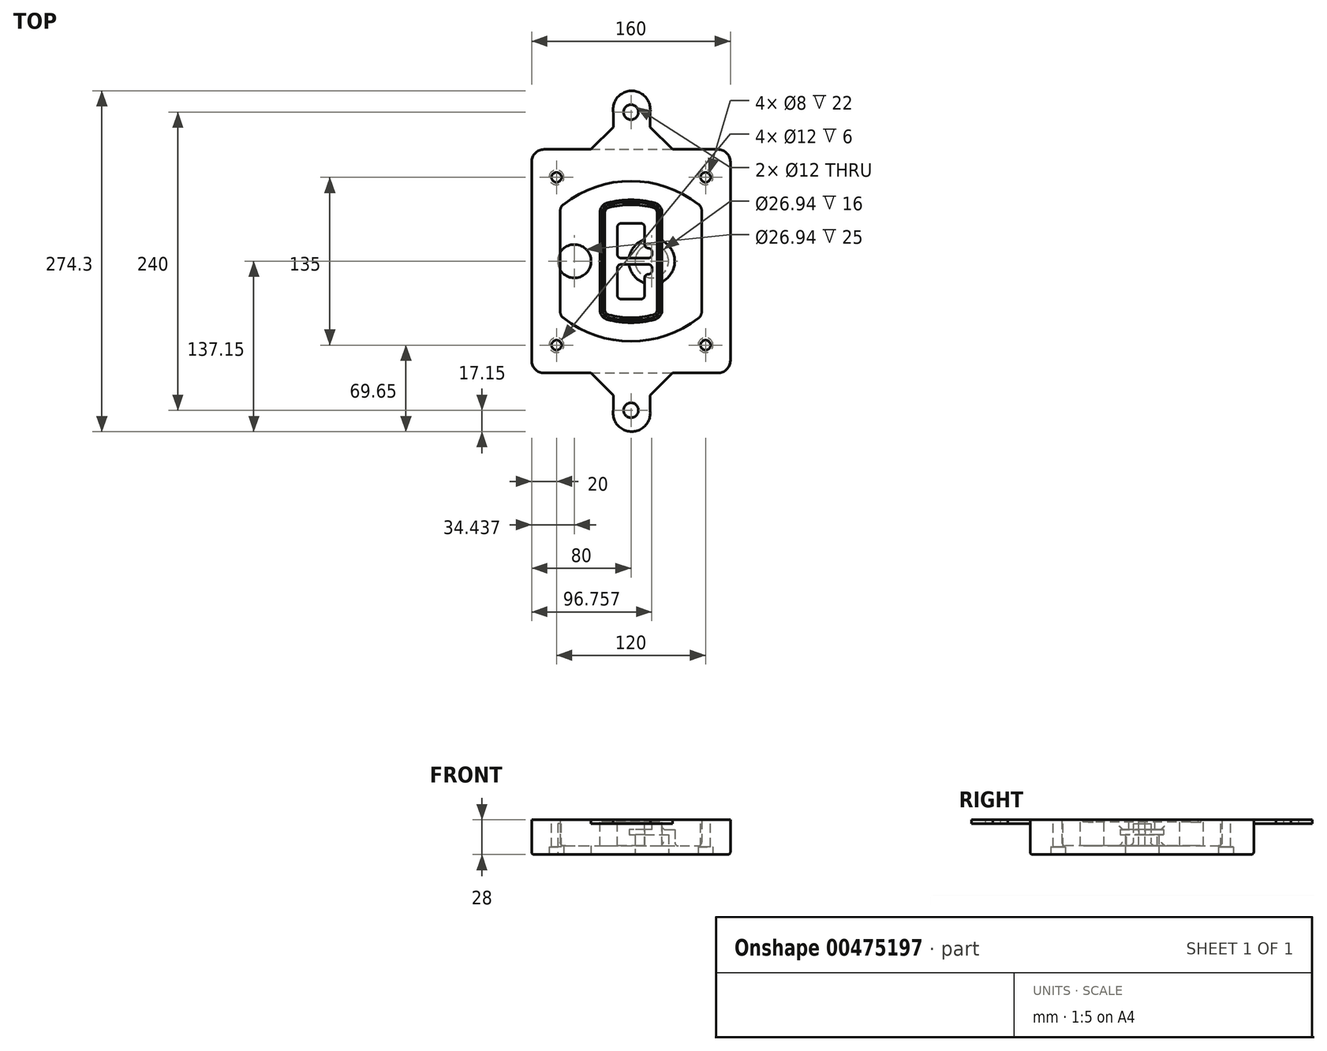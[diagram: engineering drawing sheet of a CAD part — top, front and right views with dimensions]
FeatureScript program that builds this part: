
annotation { "Feature Type Name" : "Feature", "Feature Type Description" : "" }
export const myFeature = defineFeature(function(context is Context, id is Id, definition is map)
    precondition{}
    {
        {
            var Q0;
            Q0=qCreatedBy(makeId("Top.planeOp"),FACE);
            var sketch = newSketch(context, id + "F0", { "sketchPlane" : qUnion([Q0])});
            skPoint(sketch, "E0.rect.middle", {"position": v(0, 0) * mm});
            skLineSegment(sketch, "E1.bottom", {"start": v(-70, -90) * mm, "end": v(70, -90) * mm});
            skLineSegment(sketch, "E1.top", {"start": v(-70, 90) * mm, "end": v(70, 90) * mm});
            skLineSegment(sketch, "E1.left", {"start": v(-80, -80) * mm, "end": v(-80, 80) * mm});
            skLineSegment(sketch, "E1.right", {"start": v(80, -80) * mm, "end": v(80, 80) * mm});
            skLineSegment(sketch, "E2", {"start": v(-80, 90) * mm, "end": v(80, -90) * mm, "construction": true});
            skLineSegment(sketch, "E3", {"start": v(80, 90) * mm, "end": v(-80, -90) * mm, "construction": true});
            skCircle(sketch, "E4", {"center": v(-60, 67.5) * mm, "radius": 4 * mm});
            skCircle(sketch, "E5", {"center": v(60, 67.5) * mm, "radius": 4 * mm});
            skCircle(sketch, "E6", {"center": v(60, -67.5) * mm, "radius": 4 * mm});
            skCircle(sketch, "E7", {"center": v(-60, -67.5) * mm, "radius": 4 * mm});
            skLineSegment(sketch, "E8", {"start": v(-60, 67.5) * mm, "end": v(60, 67.5) * mm, "construction": true});
            skLineSegment(sketch, "E9", {"start": v(60, 67.5) * mm, "end": v(60, -67.5) * mm, "construction": true});
            skLineSegment(sketch, "E10", {"start": v(60, -67.5) * mm, "end": v(-60, -67.5) * mm, "construction": true});
            skLineSegment(sketch, "E11", {"start": v(-60, -67.5) * mm, "end": v(-60, 67.5) * mm, "construction": true});
            skLineSegment(sketch, "E12", {"start": v(-60, 40.3) * mm, "end": v(-60, -40.3) * mm});
            skLineSegment(sketch, "E13", {"start": v(60, 40.3) * mm, "end": v(60, -40.3) * mm});
            skArc(sketch, "E14", {"start": v(56.15, 48.18) * mm, "mid": v(0, 67.5) * mm, "end": v(-56.15, 48.18) * mm});
            skArc(sketch, "E15", {"start": v(-56.15, -48.18) * mm, "mid": v(0, -67.5) * mm, "end": v(56.15, -48.18) * mm});
            skLineSegment(sketch, "E16", {"start": v(-60, 0) * mm, "end": v(60, 0) * mm, "construction": true});
            skPoint(sketch, "E17.visualSharp", {"position": v(-60, -45) * mm});
            skArc(sketch, "E17.filletArc", {"start": v(-60, -40.3) * mm, "mid": v(-58.99, -44.68) * mm, "end": v(-56.15, -48.18) * mm});
            skPoint(sketch, "E18.visualSharp", {"position": v(-60, 45) * mm});
            skArc(sketch, "E18.filletArc", {"start": v(-56.15, 48.18) * mm, "mid": v(-58.99, 44.68) * mm, "end": v(-60, 40.3) * mm});
            skPoint(sketch, "E19.visualSharp", {"position": v(60, 45) * mm});
            skArc(sketch, "E19.filletArc", {"start": v(60, 40.3) * mm, "mid": v(58.99, 44.68) * mm, "end": v(56.15, 48.18) * mm});
            skPoint(sketch, "E20.visualSharp", {"position": v(60, -45) * mm});
            skArc(sketch, "E20.filletArc", {"start": v(56.15, -48.18) * mm, "mid": v(58.99, -44.68) * mm, "end": v(60, -40.3) * mm});
            skPoint(sketch, "E21.visualSharp", {"position": v(-80, 90) * mm});
            skArc(sketch, "E21.filletArc", {"start": v(-70, 90) * mm, "mid": v(-77.07, 87.07) * mm, "end": v(-80, 80) * mm});
            skPoint(sketch, "E22.visualSharp", {"position": v(80, 90) * mm});
            skArc(sketch, "E22.filletArc", {"start": v(80, 80) * mm, "mid": v(77.07, 87.07) * mm, "end": v(70, 90) * mm});
            skPoint(sketch, "E23.visualSharp", {"position": v(80, -90) * mm});
            skArc(sketch, "E23.filletArc", {"start": v(70, -90) * mm, "mid": v(77.07, -87.07) * mm, "end": v(80, -80) * mm});
            skPoint(sketch, "E24.visualSharp", {"position": v(-80, -90) * mm});
            skArc(sketch, "E24.filletArc", {"start": v(-80, -80) * mm, "mid": v(-77.07, -87.07) * mm, "end": v(-70, -90) * mm});
            skArc(sketch, "E25.0", {"start": v(57, 40.3) * mm, "mid": v(56.3, 43.36) * mm, "end": v(54.3, 45.81) * mm});
            skLineSegment(sketch, "E25.1", {"start": v(57, 40.3) * mm, "end": v(57, -40.3) * mm});
            skArc(sketch, "E25.2", {"start": v(54.3, -45.81) * mm, "mid": v(56.3, -43.36) * mm, "end": v(57, -40.3) * mm});
            skArc(sketch, "E25.3", {"start": v(-54.3, -45.81) * mm, "mid": v(0, -64.5) * mm, "end": v(54.3, -45.81) * mm});
            skArc(sketch, "E25.4", {"start": v(-57, -40.3) * mm, "mid": v(-56.3, -43.36) * mm, "end": v(-54.3, -45.81) * mm});
            skArc(sketch, "E25.5", {"start": v(54.3, 45.81) * mm, "mid": v(0, 64.5) * mm, "end": v(-54.3, 45.81) * mm});
            skLineSegment(sketch, "E25.6", {"start": v(-57, 40.3) * mm, "end": v(-57, -40.3) * mm});
            skArc(sketch, "E25.7", {"start": v(-54.3, 45.81) * mm, "mid": v(-56.3, 43.36) * mm, "end": v(-57, 40.3) * mm});
            skArc(sketch, "E26.0", {"start": v(-58.62, 51.33) * mm, "mid": v(-62.58, 46.43) * mm, "end": v(-64, 40.3) * mm});
            skArc(sketch, "E26.1", {"start": v(58.62, 51.33) * mm, "mid": v(0, 71.5) * mm, "end": v(-58.62, 51.33) * mm});
            skArc(sketch, "E26.2", {"start": v(64, 40.3) * mm, "mid": v(62.58, 46.43) * mm, "end": v(58.62, 51.33) * mm});
            skLineSegment(sketch, "E26.3", {"start": v(64, 40.3) * mm, "end": v(64, -40.3) * mm});
            skArc(sketch, "E26.4", {"start": v(58.62, -51.33) * mm, "mid": v(62.58, -46.43) * mm, "end": v(64, -40.3) * mm});
            skLineSegment(sketch, "E26.5", {"start": v(-64, 40.3) * mm, "end": v(-64, -40.3) * mm});
            skArc(sketch, "E26.6", {"start": v(-58.62, -51.33) * mm, "mid": v(0, -71.5) * mm, "end": v(58.62, -51.33) * mm});
            skArc(sketch, "E26.7", {"start": v(-64, -40.3) * mm, "mid": v(-62.58, -46.43) * mm, "end": v(-58.62, -51.33) * mm});
            skSolve(sketch);
        }
        {
            var Q0;
            Q0=makeQuery(id+"F0.imprint","IMPRINT",FACE,{"disambiguationData":[TD([[makeQuery(id+"F0.imprint","IMPRINT",EDGE,{"derivedFrom":sQuery(id+"F0.wireOp",EDGE,"E1.bottom")}),1.0]])]});
            var Q1;
            Q1=makeQuery(id+"F0.imprint","IMPRINT",FACE,{"disambiguationData":[TD([[makeQuery(id+"F0.imprint","IMPRINT",EDGE,{"derivedFrom":sQuery(id+"F0.wireOp",EDGE,"E12")}),1.0]])]});
            var Q2;
            Q2=makeQuery(id+"F0.imprint","IMPRINT",FACE,{"disambiguationData":[TD([[makeQuery(id+"F0.imprint","IMPRINT",EDGE,{"derivedFrom":sQuery(id+"F0.wireOp",EDGE,"E25.0")}),1.0]])]});
            var Q3;
            Q3=makeQuery(id+"F0.imprint","IMPRINT",FACE,{"disambiguationData":[TD([[makeQuery(id+"F0.imprint","IMPRINT",EDGE,{"derivedFrom":sQuery(id+"F0.wireOp",EDGE,"E12")}),-1.0]])]});
            extrude(context, id + "F1", {"entities" : qUnion([Q0, Q1, Q2, Q3]), "oppositeDirection" : true, "depth" : 25 * mm});
        }
        {
            var Q0;
            Q0=makeQuery(id+"F0.imprint","IMPRINT",FACE,{"disambiguationData":[TD([[makeQuery(id+"F0.imprint","IMPRINT",EDGE,{"derivedFrom":sQuery(id+"F0.wireOp",EDGE,"E12")}),1.0]])]});
            extrude(context, id + "F2", {"entities" : qUnion([Q0]), "operationType" : NewBodyOperationType.ADD, "depth" : 3 * mm});
        }
        {
            var Q0;
            Q0=makeQuery(id+"F0.imprint","IMPRINT",FACE,{"disambiguationData":[TD([[makeQuery(id+"F0.imprint","IMPRINT",EDGE,{"derivedFrom":sQuery(id+"F0.wireOp",EDGE,"E25.0")}),1.0]])]});
            extrude(context, id + "F3", {"entities" : qUnion([Q0]), "operationType" : NewBodyOperationType.REMOVE, "oppositeDirection" : true, "depth" : 18 * mm});
        }
        {
            var Q0;
            Q0=makeQuery(id+"F2.opExtrude","CAP_FACE",FACE,{"disambiguationData":[OSD([sQuery(id+"F0.wireOp",EDGE,"E12"),sQuery(id+"F0.wireOp",EDGE,"E13"),sQuery(id+"F0.wireOp",EDGE,"E14"),sQuery(id+"F0.wireOp",EDGE,"E15"),sQuery(id+"F0.wireOp",EDGE,"E17.filletArc"),sQuery(id+"F0.wireOp",EDGE,"E18.filletArc"),sQuery(id+"F0.wireOp",EDGE,"E19.filletArc"),sQuery(id+"F0.wireOp",EDGE,"E20.filletArc"),sQuery(id+"F0.wireOp",EDGE,"E25.0"),sQuery(id+"F0.wireOp",EDGE,"E25.1"),sQuery(id+"F0.wireOp",EDGE,"E25.2"),sQuery(id+"F0.wireOp",EDGE,"E25.3"),sQuery(id+"F0.wireOp",EDGE,"E25.4"),sQuery(id+"F0.wireOp",EDGE,"E25.5"),sQuery(id+"F0.wireOp",EDGE,"E25.6"),sQuery(id+"F0.wireOp",EDGE,"E25.7")])],"isStart":false});
            var sketch = newSketch(context, id + "F4", { "sketchPlane" : qUnion([Q0])});
            skArc(sketch, "E27.0", {"start": v(-19.08, -46.97) * mm, "mid": v(0, -49.5) * mm, "end": v(19.08, -46.97) * mm});
            skArc(sketch, "E28.0", {"start": v(19.08, 46.97) * mm, "mid": v(0, 49.5) * mm, "end": v(-19.08, 46.97) * mm});
            skLineSegment(sketch, "E29", {"start": v(-25, 39.25) * mm, "end": v(-25, -39.25) * mm});
            skLineSegment(sketch, "E30", {"start": v(25, 39.25) * mm, "end": v(25, -39.25) * mm});
            skLineSegment(sketch, "E31", {"start": v(-25, 45.1) * mm, "end": v(25, 45.1) * mm, "construction": true});
            skLineSegment(sketch, "E32", {"start": v(-25, -45.1) * mm, "end": v(25, -45.1) * mm, "construction": true});
            skPoint(sketch, "E33.visualSharp", {"position": v(-25, 45.1) * mm});
            skArc(sketch, "E33.filletArc", {"start": v(-19.08, 46.97) * mm, "mid": v(-23.35, 44.11) * mm, "end": v(-25, 39.25) * mm});
            skPoint(sketch, "E34.visualSharp", {"position": v(25, 45.1) * mm});
            skArc(sketch, "E34.filletArc", {"start": v(25, 39.25) * mm, "mid": v(23.35, 44.11) * mm, "end": v(19.08, 46.97) * mm});
            skPoint(sketch, "E35.visualSharp", {"position": v(25, -45.1) * mm});
            skArc(sketch, "E35.filletArc", {"start": v(19.08, -46.97) * mm, "mid": v(23.35, -44.11) * mm, "end": v(25, -39.25) * mm});
            skPoint(sketch, "E36.visualSharp", {"position": v(-25, -45.1) * mm});
            skArc(sketch, "E36.filletArc", {"start": v(-25, -39.25) * mm, "mid": v(-23.35, -44.11) * mm, "end": v(-19.08, -46.97) * mm});
            skArc(sketch, "E37.0", {"start": v(54.3, 45.81) * mm, "mid": v(0, 64.5) * mm, "end": v(-54.3, 45.81) * mm});
            skArc(sketch, "E37.1", {"start": v(-54.3, 45.81) * mm, "mid": v(-56.3, 43.36) * mm, "end": v(-57, 40.3) * mm});
            skLineSegment(sketch, "E37.2", {"start": v(-57, 40.3) * mm, "end": v(-57, -40.3) * mm});
            skArc(sketch, "E37.3", {"start": v(-57, -40.3) * mm, "mid": v(-56.3, -43.36) * mm, "end": v(-54.3, -45.81) * mm});
            skArc(sketch, "E37.4", {"start": v(-54.3, -45.81) * mm, "mid": v(0, -64.5) * mm, "end": v(54.3, -45.81) * mm});
            skArc(sketch, "E37.5", {"start": v(54.3, -45.81) * mm, "mid": v(56.3, -43.36) * mm, "end": v(57, -40.3) * mm});
            skLineSegment(sketch, "E37.6", {"start": v(57, 40.3) * mm, "end": v(57, -40.3) * mm});
            skArc(sketch, "E37.7", {"start": v(57, 40.3) * mm, "mid": v(56.3, 43.36) * mm, "end": v(54.3, 45.81) * mm});
            skLineSegment(sketch, "E38.0", {"start": v(23, 39.25) * mm, "end": v(23, -39.25) * mm});
            skArc(sketch, "E38.1", {"start": v(18.56, -45.04) * mm, "mid": v(21.76, -42.9) * mm, "end": v(23, -39.25) * mm});
            skArc(sketch, "E38.2", {"start": v(-18.56, -45.04) * mm, "mid": v(0, -47.5) * mm, "end": v(18.56, -45.04) * mm});
            skArc(sketch, "E38.3", {"start": v(-23, -39.25) * mm, "mid": v(-21.76, -42.9) * mm, "end": v(-18.56, -45.04) * mm});
            skLineSegment(sketch, "E38.4", {"start": v(-23, 39.25) * mm, "end": v(-23, -39.25) * mm});
            skArc(sketch, "E38.5", {"start": v(23, 39.25) * mm, "mid": v(21.76, 42.9) * mm, "end": v(18.56, 45.04) * mm});
            skArc(sketch, "E38.6", {"start": v(-18.56, 45.04) * mm, "mid": v(-21.76, 42.9) * mm, "end": v(-23, 39.25) * mm});
            skArc(sketch, "E38.7", {"start": v(18.56, 45.04) * mm, "mid": v(0, 47.5) * mm, "end": v(-18.56, 45.04) * mm});
            skArc(sketch, "E39.0", {"start": v(21, 39.25) * mm, "mid": v(20.18, 41.68) * mm, "end": v(18.04, 43.1) * mm});
            skLineSegment(sketch, "E39.1", {"start": v(21, 39.25) * mm, "end": v(21, -39.25) * mm});
            skArc(sketch, "E39.2", {"start": v(18.04, -43.1) * mm, "mid": v(20.18, -41.68) * mm, "end": v(21, -39.25) * mm});
            skArc(sketch, "E39.3", {"start": v(-18.04, -43.1) * mm, "mid": v(0, -45.5) * mm, "end": v(18.04, -43.1) * mm});
            skArc(sketch, "E39.4", {"start": v(-21, -39.25) * mm, "mid": v(-20.18, -41.68) * mm, "end": v(-18.04, -43.1) * mm});
            skArc(sketch, "E39.5", {"start": v(18.04, 43.1) * mm, "mid": v(0, 45.5) * mm, "end": v(-18.04, 43.1) * mm});
            skLineSegment(sketch, "E39.6", {"start": v(-21, 39.25) * mm, "end": v(-21, -39.25) * mm});
            skArc(sketch, "E39.7", {"start": v(-18.04, 43.1) * mm, "mid": v(-20.18, 41.68) * mm, "end": v(-21, 39.25) * mm});
            skLineSegment(sketch, "E40", {"start": v(-25, 0) * mm, "end": v(25, 0) * mm, "construction": true});
            skLineSegment(sketch, "E41", {"start": v(-11, 5.5) * mm, "end": v(-11, 27.5) * mm});
            skLineSegment(sketch, "E42", {"start": v(-8, 30.5) * mm, "end": v(8, 30.5) * mm});
            skLineSegment(sketch, "E43", {"start": v(11, 27.5) * mm, "end": v(11, 13.5) * mm});
            skLineSegment(sketch, "E44", {"start": v(14, 10.5) * mm, "end": v(14, 10.5) * mm});
            skLineSegment(sketch, "E45", {"start": v(17, 7.5) * mm, "end": v(17, 5.5) * mm});
            skLineSegment(sketch, "E46", {"start": v(14, 2.5) * mm, "end": v(-8, 2.5) * mm});
            skPoint(sketch, "E47.visualSharp", {"position": v(-11, 30.5) * mm});
            skArc(sketch, "E47.filletArc", {"start": v(-8, 30.5) * mm, "mid": v(-10.12, 29.62) * mm, "end": v(-11, 27.5) * mm});
            skPoint(sketch, "E48.visualSharp", {"position": v(11, 30.5) * mm});
            skArc(sketch, "E48.filletArc", {"start": v(11, 27.5) * mm, "mid": v(10.12, 29.62) * mm, "end": v(8, 30.5) * mm});
            skPoint(sketch, "E49.visualSharp", {"position": v(11, 10.5) * mm});
            skArc(sketch, "E49.filletArc", {"start": v(11, 13.5) * mm, "mid": v(11.88, 11.38) * mm, "end": v(14, 10.5) * mm});
            skPoint(sketch, "E50.visualSharp", {"position": v(17, 10.5) * mm});
            skArc(sketch, "E50.filletArc", {"start": v(17, 7.5) * mm, "mid": v(16.12, 9.62) * mm, "end": v(14, 10.5) * mm});
            skPoint(sketch, "E51.visualSharp", {"position": v(17, 2.5) * mm});
            skArc(sketch, "E51.filletArc", {"start": v(14, 2.5) * mm, "mid": v(16.12, 3.38) * mm, "end": v(17, 5.5) * mm});
            skPoint(sketch, "E52.visualSharp", {"position": v(-11, 2.5) * mm});
            skArc(sketch, "E52.filletArc", {"start": v(-11, 5.5) * mm, "mid": v(-10.12, 3.38) * mm, "end": v(-8, 2.5) * mm});
            skLineSegment(sketch, "E53.0.MirrorCS", {"start": v(14, -2.5) * mm, "end": v(-8, -2.5) * mm});
            skArc(sketch, "E54.0.MirrorCS", {"start": v(-11, -5.5) * mm, "mid": v(-10.12, -3.38) * mm, "end": v(-8, -2.5) * mm});
            skLineSegment(sketch, "E55.0.MirrorCS", {"start": v(-11, -5.5) * mm, "end": v(-11, -27.5) * mm});
            skArc(sketch, "E56.0.MirrorCS", {"start": v(-8, -30.5) * mm, "mid": v(-10.12, -29.62) * mm, "end": v(-11, -27.5) * mm});
            skLineSegment(sketch, "E57.0.MirrorCS", {"start": v(-8, -30.5) * mm, "end": v(8, -30.5) * mm});
            skArc(sketch, "E58.0.MirrorCS", {"start": v(11, -27.5) * mm, "mid": v(10.12, -29.62) * mm, "end": v(8, -30.5) * mm});
            skLineSegment(sketch, "E59.0.MirrorCS", {"start": v(11, -27.5) * mm, "end": v(11, -13.5) * mm});
            skArc(sketch, "E60.0.MirrorCS", {"start": v(11, -13.5) * mm, "mid": v(11.88, -11.38) * mm, "end": v(14, -10.5) * mm});
            skArc(sketch, "E61.0.MirrorCS", {"start": v(17, -7.5) * mm, "mid": v(16.12, -9.62) * mm, "end": v(14, -10.5) * mm});
            skLineSegment(sketch, "E62.0.MirrorCS", {"start": v(17, -7.5) * mm, "end": v(17, -5.5) * mm});
            skArc(sketch, "E63.0.MirrorCS", {"start": v(14, -2.5) * mm, "mid": v(16.12, -3.38) * mm, "end": v(17, -5.5) * mm});
            skSolve(sketch);
        }
        {
            var Q0;
            Q0=makeQuery(id+"F4.imprint","IMPRINT",FACE,{"disambiguationData":[TD([[makeQuery(id+"F4.imprint","IMPRINT",EDGE,{"derivedFrom":sQuery(id+"F4.wireOp",EDGE,"E27.0")}),1.0]])]});
            var Q1;
            Q1=makeQuery(id+"F4.imprint","IMPRINT",FACE,{"disambiguationData":[TD([[makeQuery(id+"F4.imprint","IMPRINT",EDGE,{"derivedFrom":sQuery(id+"F4.wireOp",EDGE,"E38.0")}),-1.0]])]});
            var Q2;
            Q2=makeQuery(id+"F4.imprint","IMPRINT",FACE,{"disambiguationData":[TD([[makeQuery(id+"F4.imprint","IMPRINT",EDGE,{"derivedFrom":sQuery(id+"F4.wireOp",EDGE,"E39.0")}),1.0]])]});
            extrude(context, id + "F5", {"entities" : qUnion([Q0, Q1, Q2]), "operationType" : NewBodyOperationType.ADD, "endBound" : BoundingType.UP_TO_NEXT, "oppositeDirection" : true, "depth" : 25 * mm});
        }
        {
            var Q0;
            Q0=makeQuery(id+"F4.imprint","IMPRINT",FACE,{"disambiguationData":[TD([[makeQuery(id+"F4.imprint","IMPRINT",EDGE,{"derivedFrom":sQuery(id+"F4.wireOp",EDGE,"E38.0")}),-1.0]])]});
            extrude(context, id + "F6", {"entities" : qUnion([Q0]), "operationType" : NewBodyOperationType.REMOVE, "oppositeDirection" : true, "depth" : 2 * mm});
        }
        {
            var Q0;
            Q0=makeQuery(id+"F1.opExtrude","CAP_FACE",FACE,{"disambiguationData":[OSD([sQuery(id+"F0.wireOp",EDGE,"E1.bottom"),sQuery(id+"F0.wireOp",EDGE,"E1.top"),sQuery(id+"F0.wireOp",EDGE,"E1.left"),sQuery(id+"F0.wireOp",EDGE,"E1.right"),sQuery(id+"F0.wireOp",EDGE,"E4"),sQuery(id+"F0.wireOp",EDGE,"E5"),sQuery(id+"F0.wireOp",EDGE,"E6"),sQuery(id+"F0.wireOp",EDGE,"E7"),sQuery(id+"F0.wireOp",EDGE,"E21.filletArc"),sQuery(id+"F0.wireOp",EDGE,"E22.filletArc"),sQuery(id+"F0.wireOp",EDGE,"E23.filletArc"),sQuery(id+"F0.wireOp",EDGE,"E24.filletArc")])],"isStart":false});
            var sketch = newSketch(context, id + "F7", { "sketchPlane" : qUnion([Q0])});
            skCircle(sketch, "E64", {"center": v(16.76, 0) * mm, "radius": 13.47 * mm});
            skCircle(sketch, "E65", {"center": v(-45.56, 0) * mm, "radius": 13.47 * mm});
            skLineSegment(sketch, "E66", {"start": v(80, 0) * mm, "end": v(-80, 0) * mm});
            skCircle(sketch, "E67", {"center": v(16.76, 0) * mm, "radius": 18.47 * mm});
            skCircle(sketch, "E68", {"center": v(60, -67.5) * mm, "radius": 6 * mm});
            skCircle(sketch, "E69", {"center": v(-60, -67.5) * mm, "radius": 6 * mm});
            skCircle(sketch, "E70", {"center": v(-60, 67.5) * mm, "radius": 6 * mm});
            skCircle(sketch, "E71", {"center": v(60, 67.5) * mm, "radius": 6 * mm});
            skSolve(sketch);
        }
        {
            var Q0;
            {var subQ1=sQuery(id+"F7.wireOp",EDGE,"E66");var subQ4=sQuery(id+"F7.wireOp",EDGE,"E64");var subQ6=makeQuery(id+"F7.imprint","INTERSECT",VERTEX,{"disambiguationData":[OD(0.0)],"derivedFrom":[subQ4,subQ1]});Q0=makeQuery(id+"F7.imprint","IMPRINT",FACE,{"disambiguationData":[TD([[makeQuery(id+"F7.imprint","IMPRINT",EDGE,{"disambiguationData":[TD([[subQ6,-1.0]])],"derivedFrom":subQ4}),-1.0]])]});}
            var Q1;
            {var subQ0=sQuery(id+"F7.wireOp",EDGE,"E66");var subQ1=sQuery(id+"F7.wireOp",EDGE,"E64");var subQ3=makeQuery(id+"F7.imprint","INTERSECT",VERTEX,{"disambiguationData":[OD(0.0)],"derivedFrom":[subQ1,subQ0]});Q1=makeQuery(id+"F7.imprint","IMPRINT",FACE,{"disambiguationData":[TD([[makeQuery(id+"F7.imprint","IMPRINT",EDGE,{"disambiguationData":[TD([[subQ3,-1.0]])],"derivedFrom":subQ1}),1.0]])]});}
            var Q2;
            {var subQ0=sQuery(id+"F7.wireOp",EDGE,"E66");var subQ1=sQuery(id+"F7.wireOp",EDGE,"E64");var subQ3=makeQuery(id+"F7.imprint","INTERSECT",VERTEX,{"disambiguationData":[OD(0.0)],"derivedFrom":[subQ1,subQ0]});Q2=makeQuery(id+"F7.imprint","IMPRINT",FACE,{"disambiguationData":[TD([[makeQuery(id+"F7.imprint","IMPRINT",EDGE,{"disambiguationData":[TD([[subQ3,1.0]])],"derivedFrom":subQ1}),1.0]])]});}
            var Q3;
            {var subQ1=sQuery(id+"F7.wireOp",EDGE,"E66");var subQ4=sQuery(id+"F7.wireOp",EDGE,"E64");var subQ6=makeQuery(id+"F7.imprint","INTERSECT",VERTEX,{"disambiguationData":[OD(0.0)],"derivedFrom":[subQ4,subQ1]});Q3=makeQuery(id+"F7.imprint","IMPRINT",FACE,{"disambiguationData":[TD([[makeQuery(id+"F7.imprint","IMPRINT",EDGE,{"disambiguationData":[TD([[subQ6,1.0]])],"derivedFrom":subQ4}),-1.0]])]});}
            extrude(context, id + "F8", {"entities" : qUnion([Q0, Q1, Q2, Q3]), "operationType" : NewBodyOperationType.ADD, "oppositeDirection" : true, "depth" : 20 * mm});
        }
        {
            var Q0;
            {var subQ0=sQuery(id+"F7.wireOp",EDGE,"E66");var subQ1=sQuery(id+"F7.wireOp",EDGE,"E64");var subQ3=makeQuery(id+"F7.imprint","INTERSECT",VERTEX,{"disambiguationData":[OD(0.0)],"derivedFrom":[subQ1,subQ0]});Q0=makeQuery(id+"F7.imprint","IMPRINT",FACE,{"disambiguationData":[TD([[makeQuery(id+"F7.imprint","IMPRINT",EDGE,{"disambiguationData":[TD([[subQ3,-1.0]])],"derivedFrom":subQ1}),1.0]])]});}
            var Q1;
            {var subQ0=sQuery(id+"F7.wireOp",EDGE,"E66");var subQ1=sQuery(id+"F7.wireOp",EDGE,"E64");var subQ3=makeQuery(id+"F7.imprint","INTERSECT",VERTEX,{"disambiguationData":[OD(0.0)],"derivedFrom":[subQ1,subQ0]});Q1=makeQuery(id+"F7.imprint","IMPRINT",FACE,{"disambiguationData":[TD([[makeQuery(id+"F7.imprint","IMPRINT",EDGE,{"disambiguationData":[TD([[subQ3,1.0]])],"derivedFrom":subQ1}),1.0]])]});}
            extrude(context, id + "F9", {"entities" : qUnion([Q0, Q1]), "operationType" : NewBodyOperationType.REMOVE, "oppositeDirection" : true, "depth" : 16 * mm});
        }
        {
            var Q0;
            {var subQ0=sQuery(id+"F7.wireOp",EDGE,"E66");var subQ1=sQuery(id+"F7.wireOp",EDGE,"E65");var subQ3=makeQuery(id+"F7.imprint","INTERSECT",VERTEX,{"disambiguationData":[OD(0.0)],"derivedFrom":[subQ1,subQ0]});Q0=makeQuery(id+"F7.imprint","IMPRINT",FACE,{"disambiguationData":[TD([[makeQuery(id+"F7.imprint","IMPRINT",EDGE,{"disambiguationData":[TD([[subQ3,-1.0]])],"derivedFrom":subQ1}),1.0]])]});}
            var Q1;
            {var subQ0=sQuery(id+"F7.wireOp",EDGE,"E66");var subQ1=sQuery(id+"F7.wireOp",EDGE,"E65");var subQ3=makeQuery(id+"F7.imprint","INTERSECT",VERTEX,{"disambiguationData":[OD(0.0)],"derivedFrom":[subQ1,subQ0]});Q1=makeQuery(id+"F7.imprint","IMPRINT",FACE,{"disambiguationData":[TD([[makeQuery(id+"F7.imprint","IMPRINT",EDGE,{"disambiguationData":[TD([[subQ3,1.0]])],"derivedFrom":subQ1}),1.0]])]});}
            extrude(context, id + "F10", {"entities" : qUnion([Q0, Q1]), "operationType" : NewBodyOperationType.REMOVE, "oppositeDirection" : true, "depth" : 25 * mm});
        }
        {
            var Q0;
            Q0=makeQuery(id+"F7.imprint","IMPRINT",FACE,{"disambiguationData":[TD([[makeQuery(id+"F7.imprint","IMPRINT",EDGE,{"derivedFrom":sQuery(id+"F7.wireOp",EDGE,"E68")}),1.0]])]});
            var Q1;
            Q1=makeQuery(id+"F7.imprint","IMPRINT",FACE,{"disambiguationData":[TD([[makeQuery(id+"F7.imprint","IMPRINT",EDGE,{"derivedFrom":makeQuery(id+"F1.opExtrude","CAP_EDGE",EDGE,{"disambiguationData":[OSD([sQuery(id+"F0.wireOp",EDGE,"E5")])],"isStart":false})}),-1.0]])]});
            var Q2;
            Q2=makeQuery(id+"F7.imprint","IMPRINT",FACE,{"disambiguationData":[TD([[makeQuery(id+"F7.imprint","IMPRINT",EDGE,{"derivedFrom":sQuery(id+"F7.wireOp",EDGE,"E69")}),1.0]])]});
            var Q3;
            Q3=makeQuery(id+"F7.imprint","IMPRINT",FACE,{"disambiguationData":[TD([[makeQuery(id+"F7.imprint","IMPRINT",EDGE,{"derivedFrom":makeQuery(id+"F1.opExtrude","CAP_EDGE",EDGE,{"disambiguationData":[OSD([sQuery(id+"F0.wireOp",EDGE,"E4")])],"isStart":false})}),-1.0]])]});
            var Q4;
            Q4=makeQuery(id+"F7.imprint","IMPRINT",FACE,{"disambiguationData":[TD([[makeQuery(id+"F7.imprint","IMPRINT",EDGE,{"derivedFrom":sQuery(id+"F7.wireOp",EDGE,"E70")}),1.0]])]});
            var Q5;
            Q5=makeQuery(id+"F7.imprint","IMPRINT",FACE,{"disambiguationData":[TD([[makeQuery(id+"F7.imprint","IMPRINT",EDGE,{"derivedFrom":makeQuery(id+"F1.opExtrude","CAP_EDGE",EDGE,{"disambiguationData":[OSD([sQuery(id+"F0.wireOp",EDGE,"E7")])],"isStart":false})}),-1.0]])]});
            var Q6;
            Q6=makeQuery(id+"F7.imprint","IMPRINT",FACE,{"disambiguationData":[TD([[makeQuery(id+"F7.imprint","IMPRINT",EDGE,{"derivedFrom":sQuery(id+"F7.wireOp",EDGE,"E71")}),1.0]])]});
            var Q7;
            Q7=makeQuery(id+"F7.imprint","IMPRINT",FACE,{"disambiguationData":[TD([[makeQuery(id+"F7.imprint","IMPRINT",EDGE,{"derivedFrom":makeQuery(id+"F1.opExtrude","CAP_EDGE",EDGE,{"disambiguationData":[OSD([sQuery(id+"F0.wireOp",EDGE,"E6")])],"isStart":false})}),-1.0]])]});
            extrude(context, id + "F11", {"entities" : qUnion([Q0, Q1, Q2, Q3, Q4, Q5, Q6, Q7]), "operationType" : NewBodyOperationType.REMOVE, "oppositeDirection" : true, "depth" : 6 * mm});
        }
        {
            var Q0;
            Q0=makeQuery(id+"F9.boolean.opBoolean","COPY",FACE,{"derivedFrom":makeQuery(id+"F9.opExtrude","CAP_FACE",FACE,{"disambiguationData":[OSD([sQuery(id+"F7.wireOp",EDGE,"E64")])],"isStart":false})});
            var sketch = newSketch(context, id + "F12", { "sketchPlane" : qUnion([Q0])});
            skArc(sketch, "E72.0", {"start": v(11, 17.55) * mm, "mid": v(2.57, 11.82) * mm, "end": v(-1.54, 2.5) * mm});
            skArc(sketch, "E72.1", {"start": v(-1.54, -2.5) * mm, "mid": v(2.57, -11.82) * mm, "end": v(11, -17.55) * mm});
            skLineSegment(sketch, "E73", {"start": v(-1.54, -2.5) * mm, "end": v(14, -2.5) * mm});
            skLineSegment(sketch, "E74.0", {"start": v(14, 2.5) * mm, "end": v(-1.54, 2.5) * mm});
            skArc(sketch, "E74.1", {"start": v(14, 2.5) * mm, "mid": v(16.12, 3.38) * mm, "end": v(17, 5.5) * mm});
            skLineSegment(sketch, "E74.2", {"start": v(17, 7.5) * mm, "end": v(17, 5.5) * mm});
            skArc(sketch, "E74.3", {"start": v(17, 7.5) * mm, "mid": v(16.12, 9.62) * mm, "end": v(14, 10.5) * mm});
            skArc(sketch, "E74.4", {"start": v(11, 13.5) * mm, "mid": v(11.88, 11.38) * mm, "end": v(14, 10.5) * mm});
            skLineSegment(sketch, "E74.5", {"start": v(11, 17.55) * mm, "end": v(11, 13.5) * mm});
            skLineSegment(sketch, "E74.7", {"start": v(14, -2.5) * mm, "end": v(-1.54, -2.5) * mm});
            skArc(sketch, "E74.8", {"start": v(14, -2.5) * mm, "mid": v(16.12, -3.38) * mm, "end": v(17, -5.5) * mm});
            skLineSegment(sketch, "E74.9", {"start": v(17, -7.5) * mm, "end": v(17, -5.5) * mm});
            skArc(sketch, "E74.10", {"start": v(17, -7.5) * mm, "mid": v(16.12, -9.62) * mm, "end": v(14, -10.5) * mm});
            skArc(sketch, "E74.11", {"start": v(11, -13.5) * mm, "mid": v(11.88, -11.38) * mm, "end": v(14, -10.5) * mm});
            skLineSegment(sketch, "E74.12", {"start": v(11, -17.55) * mm, "end": v(11, -13.5) * mm});
            skPoint(sketch, "E75.orphan", {"position": v(11, -27.5) * mm});
            skPoint(sketch, "E76.orphan", {"position": v(-8, -2.5) * mm});
            skPoint(sketch, "E77.orphan", {"position": v(-8, 2.5) * mm});
            skPoint(sketch, "E78.orphan", {"position": v(11, 27.5) * mm});
            skSolve(sketch);
        }
        {
            var Q0;
            {var subQ7=sQuery(id+"F12.wireOp",EDGE,"E72.0");var subQ14=sQuery(id+"F12.wireOp",EDGE,"E72.1");var subQ16=sQuery(id+"F12.wireOp",EDGE,"E74.1");var subQ18=sQuery(id+"F12.wireOp",EDGE,"E74.8");Q0=qUnion([makeQuery(id+"F12.imprint","IMPRINT",FACE,{"disambiguationData":[TD([[makeQuery(id+"F12.imprint","IMPRINT",EDGE,{"derivedFrom":subQ7}),1.0]])]}),makeQuery(id+"F12.imprint","IMPRINT",FACE,{"disambiguationData":[TD([[makeQuery(id+"F12.imprint","IMPRINT",EDGE,{"derivedFrom":subQ14}),1.0]])]}),makeQuery(id+"F12.imprint","IMPRINT",FACE,{"disambiguationData":[TD([[makeQuery(id+"F12.imprint","IMPRINT",EDGE,{"derivedFrom":subQ16}),1.0]])]}),makeQuery(id+"F12.imprint","IMPRINT",FACE,{"disambiguationData":[TD([[makeQuery(id+"F12.imprint","IMPRINT",EDGE,{"derivedFrom":subQ18}),-1.0]])]})]);}
            var Q1;
            Q1=makeQuery(id+"F5.boolean.opBoolean","SPLIT",FACE,{"disambiguationData":[TD([makeQuery(id+"F5.opExtrude","SWEPT_FACE",FACE,{"disambiguationData":[OSD([sQuery(id+"F4.wireOp",EDGE,"E41")])]})])],"derivedFrom":makeQuery(id+"F3.boolean.opBoolean","COPY",FACE,{"derivedFrom":makeQuery(id+"F3.opExtrude","CAP_FACE",FACE,{"disambiguationData":[OSD([sQuery(id+"F0.wireOp",EDGE,"E25.0"),sQuery(id+"F0.wireOp",EDGE,"E25.1"),sQuery(id+"F0.wireOp",EDGE,"E25.2"),sQuery(id+"F0.wireOp",EDGE,"E25.3"),sQuery(id+"F0.wireOp",EDGE,"E25.4"),sQuery(id+"F0.wireOp",EDGE,"E25.5"),sQuery(id+"F0.wireOp",EDGE,"E25.6"),sQuery(id+"F0.wireOp",EDGE,"E25.7")])],"isStart":false})})});
            extrude(context, id + "F13", {"entities" : qUnion([Q0]), "operationType" : NewBodyOperationType.REMOVE, "endBound" : BoundingType.UP_TO_SURFACE, "endBoundEntityFace" : qUnion([Q1]), "depth" : 25 * mm});
        }
        {
            var Q0;
            Q0=makeQuery(id+"F3.boolean.opBoolean","COPY",EDGE,{"derivedFrom":makeQuery(id+"F3.opExtrude","CAP_EDGE",EDGE,{"disambiguationData":[OSD([sQuery(id+"F0.wireOp",EDGE,"E25.6")])],"isStart":false})});
            var Q1;
            Q1=makeQuery(id+"F8.boolean.opBoolean","INTERSECT",EDGE,{"derivedFrom":[makeQuery(id+"F5.opExtrude","SWEPT_FACE",FACE,{"disambiguationData":[OSD([sQuery(id+"F4.wireOp",EDGE,"E30")])]}),makeQuery(id+"F8.opExtrude","CAP_FACE",FACE,{"disambiguationData":[OSD([sQuery(id+"F7.wireOp",EDGE,"E67")])],"isStart":false})]});
            var Q2;
            Q2=makeQuery(id+"F8.boolean.opBoolean","INTERSECT",EDGE,{"disambiguationData":[OD(1.0)],"derivedFrom":[makeQuery(id+"F5.opExtrude","SWEPT_FACE",FACE,{"disambiguationData":[OSD([sQuery(id+"F4.wireOp",EDGE,"E30")])]}),makeQuery(id+"F8.opExtrude","SWEPT_FACE",FACE,{"disambiguationData":[OSD([sQuery(id+"F7.wireOp",EDGE,"E67")])]})]});
            var Q3;
            {var subQ0=sQuery(id+"F4.wireOp",EDGE,"E30");Q3=makeQuery(id+"F8.boolean.opBoolean","SPLIT",EDGE,{"disambiguationData":[TD([makeQuery(id+"F5.opExtrude","SWEPT_FACE",FACE,{"disambiguationData":[OSD([sQuery(id+"F4.wireOp",EDGE,"E35.filletArc")])]})])],"derivedFrom":makeQuery(id+"F5.opExtrude","CAP_EDGE",EDGE,{"disambiguationData":[OSD([subQ0])],"isStart":false})});}
            var Q4;
            {var subQ0=sQuery(id+"F0.wireOp",EDGE,"E25.7");var subQ1=sQuery(id+"F0.wireOp",EDGE,"E25.1");var subQ2=sQuery(id+"F0.wireOp",EDGE,"E25.6");var subQ3=sQuery(id+"F0.wireOp",EDGE,"E25.5");var subQ4=sQuery(id+"F0.wireOp",EDGE,"E25.4");var subQ5=sQuery(id+"F0.wireOp",EDGE,"E25.0");var subQ6=sQuery(id+"F0.wireOp",EDGE,"E25.2");var subQ7=sQuery(id+"F0.wireOp",EDGE,"E25.3");Q4=makeQuery(id+"F8.boolean.opBoolean","INTERSECT",EDGE,{"derivedFrom":[makeQuery(id+"F5.boolean.opBoolean","SPLIT",FACE,{"disambiguationData":[TD([makeQuery(id+"F2.opExtrude","SWEPT_FACE",FACE,{"disambiguationData":[OSD([subQ5])]})])],"derivedFrom":makeQuery(id+"F3.boolean.opBoolean","COPY",FACE,{"derivedFrom":makeQuery(id+"F3.opExtrude","CAP_FACE",FACE,{"disambiguationData":[OSD([subQ5,subQ1,subQ6,subQ7,subQ4,subQ3,subQ2,subQ0])],"isStart":false})})}),makeQuery(id+"F8.opExtrude","SWEPT_FACE",FACE,{"disambiguationData":[OSD([sQuery(id+"F7.wireOp",EDGE,"E67")])]})]});}
            var Q5;
            Q5=makeQuery(id+"F8.boolean.opBoolean","INTERSECT",EDGE,{"disambiguationData":[OD(0.0)],"derivedFrom":[makeQuery(id+"F5.opExtrude","SWEPT_FACE",FACE,{"disambiguationData":[OSD([sQuery(id+"F4.wireOp",EDGE,"E30")])]}),makeQuery(id+"F8.opExtrude","SWEPT_FACE",FACE,{"disambiguationData":[OSD([sQuery(id+"F7.wireOp",EDGE,"E67")])]})]});
            fillet(context, id + "F14", {"entities" : qUnion([Q0, Q1, Q2, Q3, Q4, Q5]), "radius" : 3 * mm, "tangentPropagation" : true, "allowEdgeOverflow" : false});
        }
        {
            var Q0;
            Q0=makeQuery(id+"F1.opExtrude","CAP_EDGE",EDGE,{"disambiguationData":[OSD([sQuery(id+"F0.wireOp",EDGE,"E1.bottom")])],"isStart":false});
            fillet(context, id + "F15", {"entities" : qUnion([Q0]), "radius" : 2 * mm, "tangentPropagation" : true, "allowEdgeOverflow" : false});
        }
        {
            var Q0;
            {var subQ0=sQuery(id+"F0.wireOp",EDGE,"E21.filletArc");var subQ1=sQuery(id+"F0.wireOp",EDGE,"E7");var subQ2=sQuery(id+"F0.wireOp",EDGE,"E6");var subQ3=sQuery(id+"F0.wireOp",EDGE,"E5");var subQ4=sQuery(id+"F0.wireOp",EDGE,"E4");var subQ5=sQuery(id+"F0.wireOp",EDGE,"E22.filletArc");var subQ6=sQuery(id+"F0.wireOp",EDGE,"E1.bottom");var subQ7=sQuery(id+"F0.wireOp",EDGE,"E1.right");var subQ8=sQuery(id+"F0.wireOp",EDGE,"E1.top");var subQ9=sQuery(id+"F0.wireOp",EDGE,"E1.left");var subQ10=sQuery(id+"F0.wireOp",EDGE,"E23.filletArc");var subQ11=sQuery(id+"F0.wireOp",EDGE,"E24.filletArc");Q0=makeQuery(id+"F2.boolean.opBoolean","SPLIT",FACE,{"disambiguationData":[TD([makeQuery(id+"F1.opExtrude","SWEPT_FACE",FACE,{"disambiguationData":[OSD([subQ6])]})])],"derivedFrom":makeQuery(id+"F1.opExtrude","CAP_FACE",FACE,{"disambiguationData":[OSD([subQ6,subQ8,subQ9,subQ7,subQ4,subQ3,subQ2,subQ1,subQ0,subQ5,subQ10,subQ11])],"isStart":true})});}
            var sketch = newSketch(context, id + "F16", { "sketchPlane" : qUnion([Q0])});
            skCircle(sketch, "E79.0", {"center": v(-60, 67.5) * mm, "radius": 4 * mm});
            skArc(sketch, "E80.0", {"start": v(-70, 90) * mm, "mid": v(-77.07, 87.07) * mm, "end": v(-80, 80) * mm});
            skLineSegment(sketch, "E81.0", {"start": v(-70, 90) * mm, "end": v(70, 90) * mm});
            skCircle(sketch, "E82.0", {"center": v(60, 67.5) * mm, "radius": 4 * mm});
            skArc(sketch, "E83.0", {"start": v(80, 80) * mm, "mid": v(77.07, 87.07) * mm, "end": v(70, 90) * mm});
            skLineSegment(sketch, "E84.0", {"start": v(80, -80) * mm, "end": v(80, 80) * mm});
            skLineSegment(sketch, "E85.0", {"start": v(-80, -80) * mm, "end": v(-80, 80) * mm});
            skArc(sketch, "E86.0", {"start": v(-56.15, 48.18) * mm, "mid": v(-58.99, 44.68) * mm, "end": v(-60, 40.3) * mm});
            skArc(sketch, "E87.0", {"start": v(56.15, 48.18) * mm, "mid": v(0, 67.5) * mm, "end": v(-56.15, 48.18) * mm});
            skLineSegment(sketch, "E88.0", {"start": v(-60, 40.3) * mm, "end": v(-60, -40.3) * mm});
            skLineSegment(sketch, "E89.0", {"start": v(60, 40.3) * mm, "end": v(60, -40.3) * mm});
            skArc(sketch, "E90.0", {"start": v(60, 40.3) * mm, "mid": v(58.99, 44.68) * mm, "end": v(56.15, 48.18) * mm});
            skArc(sketch, "E91.0", {"start": v(70, -90) * mm, "mid": v(77.07, -87.07) * mm, "end": v(80, -80) * mm});
            skLineSegment(sketch, "E92.0", {"start": v(-70, -90) * mm, "end": v(70, -90) * mm});
            skArc(sketch, "E93.0", {"start": v(-80, -80) * mm, "mid": v(-77.07, -87.07) * mm, "end": v(-70, -90) * mm});
            skArc(sketch, "E94.0", {"start": v(-56.15, -48.18) * mm, "mid": v(0, -67.5) * mm, "end": v(56.15, -48.18) * mm});
            skArc(sketch, "E95.0", {"start": v(-60, -40.3) * mm, "mid": v(-58.99, -44.68) * mm, "end": v(-56.15, -48.18) * mm});
            skArc(sketch, "E96.0", {"start": v(56.15, -48.18) * mm, "mid": v(58.99, -44.68) * mm, "end": v(60, -40.3) * mm});
            skCircle(sketch, "E97.0", {"center": v(-60, -67.5) * mm, "radius": 4 * mm});
            skCircle(sketch, "E98.0", {"center": v(60, -67.5) * mm, "radius": 4 * mm});
            skLineSegment(sketch, "E99", {"start": v(0, 90) * mm, "end": v(0, 120) * mm, "construction": true});
            skCircle(sketch, "E100", {"center": v(0, 120) * mm, "radius": 6 * mm});
            skArc(sketch, "E101", {"start": v(15.4, 120) * mm, "mid": v(0.55, 137.15) * mm, "end": v(-14.3, 120) * mm});
            skLineSegment(sketch, "E102", {"start": v(-14.3, 120) * mm, "end": v(-14.3, 108) * mm});
            skLineSegment(sketch, "E103", {"start": v(15.4, 120) * mm, "end": v(15.4, 108) * mm});
            skLineSegment(sketch, "E104", {"start": v(-14.3, 108) * mm, "end": v(-32.3, 90) * mm});
            skLineSegment(sketch, "E105", {"start": v(15.4, 108) * mm, "end": v(33.4, 90) * mm});
            skLineSegment(sketch, "E106", {"start": v(80, 0) * mm, "end": v(-80, 0) * mm, "construction": true});
            skLineSegment(sketch, "E107.MirrorCS", {"start": v(-14.3, -108) * mm, "end": v(-32.3, -90) * mm});
            skLineSegment(sketch, "E108.MirrorCS", {"start": v(-14.3, -120) * mm, "end": v(-14.3, -108) * mm});
            skArc(sketch, "E109.MirrorCS", {"start": v(15.4, -120) * mm, "mid": v(0.55, -137.15) * mm, "end": v(-14.3, -120) * mm});
            skCircle(sketch, "E110.MirrorC", {"center": v(0, -120) * mm, "radius": 6 * mm});
            skLineSegment(sketch, "E111.MirrorCS", {"start": v(15.4, -120) * mm, "end": v(15.4, -108) * mm});
            skLineSegment(sketch, "E112.MirrorCS", {"start": v(15.4, -108) * mm, "end": v(33.4, -90) * mm});
            skLineSegment(sketch, "E113.MirrorCS", {"start": v(0, -90) * mm, "end": v(0, -120) * mm, "construction": true});
            skSolve(sketch);
        }
        {
            var Q0;
            Q0=makeQuery(id+"F16.imprint","IMPRINT",FACE,{"disambiguationData":[TD([[makeQuery(id+"F16.imprint","IMPRINT",EDGE,{"derivedFrom":sQuery(id+"F16.wireOp",EDGE,"E79.0")}),-1.0]])]});
            var Q1;
            Q1=makeQuery(id+"F16.imprint","IMPRINT",FACE,{"disambiguationData":[TD([[makeQuery(id+"F16.imprint","IMPRINT",EDGE,{"derivedFrom":sQuery(id+"F16.wireOp",EDGE,"E100")}),-1.0]])]});
            var Q2;
            {var subQ0=sQuery(id+"F16.wireOp",EDGE,"E107.MirrorCS");Q2=makeQuery(id+"F16.imprint","IMPRINT",FACE,{"disambiguationData":[TD([[makeQuery(id+"F16.imprint","IMPRINT",EDGE,{"derivedFrom":subQ0}),-1.0]])]});}
            var Q3;
            Q3=makeQuery(id+"F2.opExtrude","CAP_FACE",FACE,{"disambiguationData":[OSD([sQuery(id+"F0.wireOp",EDGE,"E12"),sQuery(id+"F0.wireOp",EDGE,"E13"),sQuery(id+"F0.wireOp",EDGE,"E14"),sQuery(id+"F0.wireOp",EDGE,"E15"),sQuery(id+"F0.wireOp",EDGE,"E17.filletArc"),sQuery(id+"F0.wireOp",EDGE,"E18.filletArc"),sQuery(id+"F0.wireOp",EDGE,"E19.filletArc"),sQuery(id+"F0.wireOp",EDGE,"E20.filletArc"),sQuery(id+"F0.wireOp",EDGE,"E25.0"),sQuery(id+"F0.wireOp",EDGE,"E25.1"),sQuery(id+"F0.wireOp",EDGE,"E25.2"),sQuery(id+"F0.wireOp",EDGE,"E25.3"),sQuery(id+"F0.wireOp",EDGE,"E25.4"),sQuery(id+"F0.wireOp",EDGE,"E25.5"),sQuery(id+"F0.wireOp",EDGE,"E25.6"),sQuery(id+"F0.wireOp",EDGE,"E25.7")])],"isStart":false});
            extrude(context, id + "F17", {"entities" : qUnion([Q0, Q1, Q2]), "operationType" : NewBodyOperationType.ADD, "endBound" : BoundingType.UP_TO_SURFACE, "endBoundEntityFace" : qUnion([Q3]), "depth" : 25 * mm});
        }
    });
